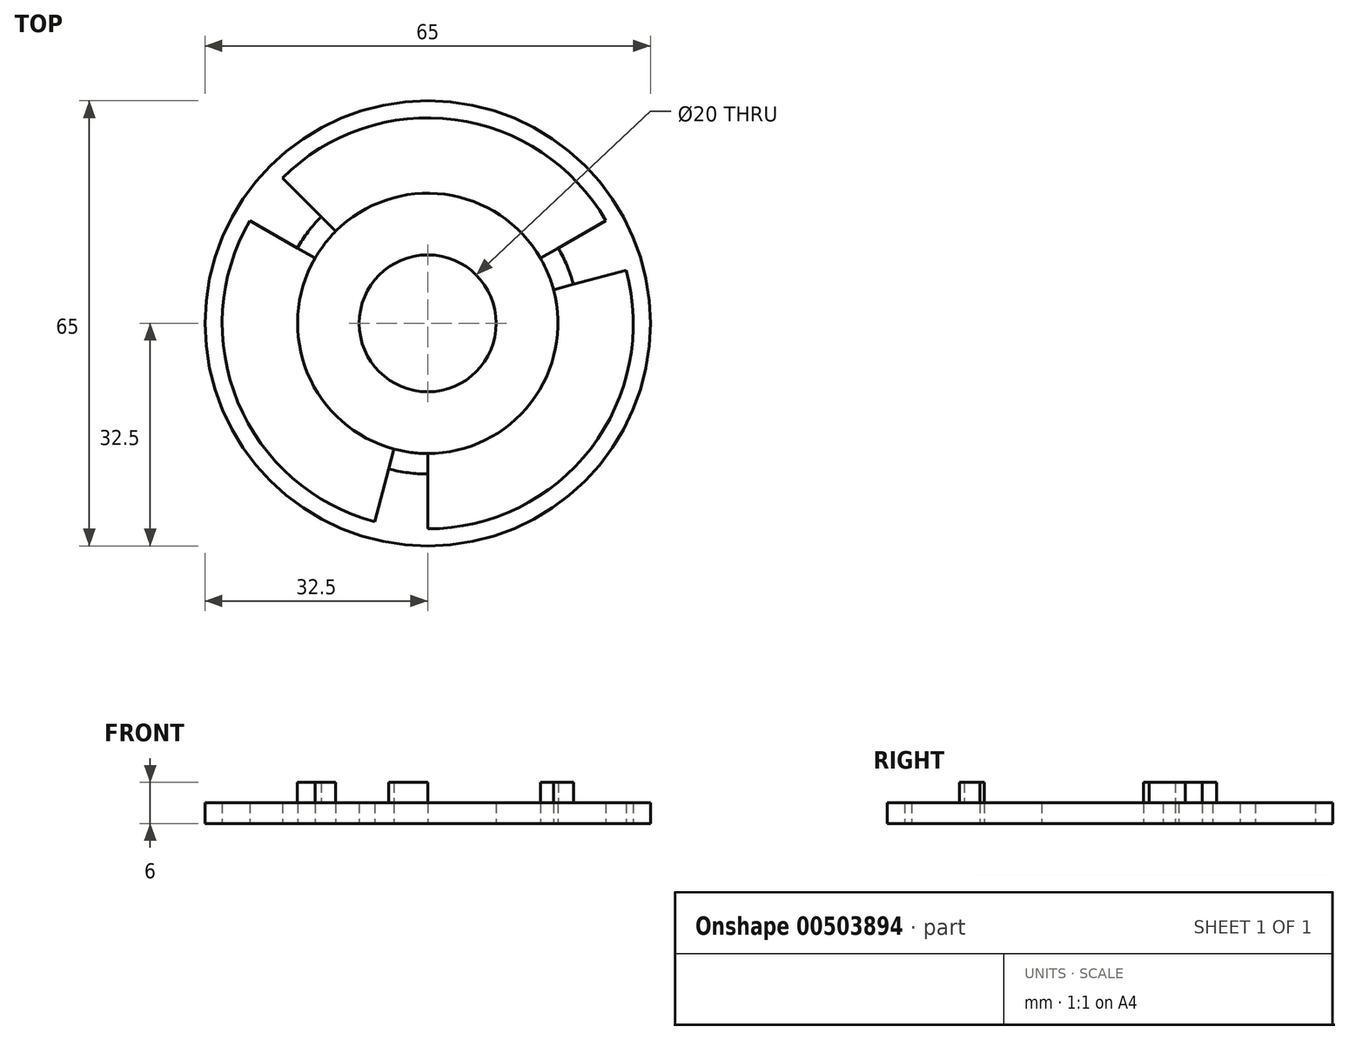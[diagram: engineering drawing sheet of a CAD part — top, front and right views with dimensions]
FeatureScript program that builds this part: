
annotation { "Feature Type Name" : "Feature", "Feature Type Description" : "" }
export const myFeature = defineFeature(function(context is Context, id is Id, definition is map)
    precondition{}
    {
        {
            var Q0;
            Q0=qCreatedBy(makeId("Top.planeOp"),FACE);
            var sketch = newSketch(context, id + "F0", { "sketchPlane" : qUnion([Q0])});
            skCircle(sketch, "E0", {"center": v(0, 0) * mm, "radius": 32.5 * mm});
            skArc(sketch, "E1", {"start": v(-25.98, 15) * mm, "mid": v(-27.72, -11.48) * mm, "end": v(-7.76, -28.98) * mm});
            skArc(sketch, "E2", {"start": v(-16.45, 9.5) * mm, "mid": v(-17.55, -7.27) * mm, "end": v(-4.92, -18.35) * mm});
            skCircle(sketch, "E3", {"center": v(0, 0) * mm, "radius": 10 * mm});
            skLineSegment(sketch, "E4", {"start": v(0, -19) * mm, "end": v(0, -30) * mm});
            skLineSegment(sketch, "E5.trimOffspring", {"start": v(-4.92, -18.35) * mm, "end": v(-7.76, -28.98) * mm});
            skLineSegment(sketch, "E6.1.0", {"start": v(16.45, 9.5) * mm, "end": v(25.98, 15) * mm});
            skLineSegment(sketch, "E6.1.1", {"start": v(18.35, 4.92) * mm, "end": v(28.98, 7.76) * mm});
            skLineSegment(sketch, "E6.2.0", {"start": v(-16.45, 9.5) * mm, "end": v(-25.98, 15) * mm});
            skLineSegment(sketch, "E6.2.1", {"start": v(-13.44, 13.44) * mm, "end": v(-21.21, 21.21) * mm});
            skArc(sketch, "E7.trimOffspring", {"start": v(16.45, 9.5) * mm, "mid": v(2.48, 18.84) * mm, "end": v(-13.44, 13.44) * mm});
            skArc(sketch, "E8.trimOffspring", {"start": v(25.98, 15) * mm, "mid": v(3.92, 29.74) * mm, "end": v(-21.21, 21.21) * mm});
            skArc(sketch, "E9.trimOffspring", {"start": v(0, -19) * mm, "mid": v(15.07, -11.57) * mm, "end": v(18.35, 4.92) * mm});
            skArc(sketch, "E10.trimOffspring", {"start": v(0, -30) * mm, "mid": v(23.8, -18.26) * mm, "end": v(28.98, 7.76) * mm});
            skSolve(sketch);
        }
        {
            var Q0;
            Q0 = qSketchRegion(id + "F0", true);
            extrude(context, id + "F1", {"entities" : qUnion([Q0]), "depth" : 3 * mm});
        }
        {
            var Q0;
            Q0=makeQuery(id+"F1.opExtrude","CAP_FACE",FACE,{"disambiguationData":[OSD([sQuery(id+"F0.wireOp",EDGE,"E0"),sQuery(id+"F0.wireOp",EDGE,"E1"),sQuery(id+"F0.wireOp",EDGE,"E2"),sQuery(id+"F0.wireOp",EDGE,"E3"),sQuery(id+"F0.wireOp",EDGE,"E4"),sQuery(id+"F0.wireOp",EDGE,"E5.trimOffspring"),sQuery(id+"F0.wireOp",EDGE,"E6.1.0"),sQuery(id+"F0.wireOp",EDGE,"E6.1.1"),sQuery(id+"F0.wireOp",EDGE,"E6.2.0"),sQuery(id+"F0.wireOp",EDGE,"E6.2.1"),sQuery(id+"F0.wireOp",EDGE,"E7.trimOffspring"),sQuery(id+"F0.wireOp",EDGE,"E8.trimOffspring"),sQuery(id+"F0.wireOp",EDGE,"E9.trimOffspring"),sQuery(id+"F0.wireOp",EDGE,"E10.trimOffspring")])],"isStart":false});
            var sketch = newSketch(context, id + "F2", { "sketchPlane" : qUnion([Q0])});
            skArc(sketch, "E11", {"start": v(-4.92, -18.35) * mm, "mid": v(-2.48, -18.84) * mm, "end": v(0, -19) * mm});
            skArc(sketch, "E12", {"start": v(-5.7, -21.25) * mm, "mid": v(-2.87, -21.81) * mm, "end": v(0, -22) * mm});
            skLineSegment(sketch, "E13.0", {"start": v(-16.45, 9.5) * mm, "end": v(-19.05, 11) * mm});
            skLineSegment(sketch, "E14.0", {"start": v(-13.44, 13.44) * mm, "end": v(-15.56, 15.56) * mm});
            skLineSegment(sketch, "E15.0", {"start": v(16.45, 9.5) * mm, "end": v(19.05, 11) * mm});
            skLineSegment(sketch, "E16.0", {"start": v(18.35, 4.92) * mm, "end": v(21.25, 5.7) * mm});
            skLineSegment(sketch, "E17.0", {"start": v(0, -19) * mm, "end": v(0, -22) * mm});
            skLineSegment(sketch, "E18.0", {"start": v(-4.92, -18.35) * mm, "end": v(-5.7, -21.25) * mm});
            skPoint(sketch, "E19.orphan", {"position": v(-25.98, 15) * mm});
            skPoint(sketch, "E20.orphan", {"position": v(-21.21, 21.21) * mm});
            skPoint(sketch, "E21.orphan", {"position": v(25.98, 15) * mm});
            skPoint(sketch, "E22.orphan", {"position": v(28.98, 7.76) * mm});
            skPoint(sketch, "E23.orphan", {"position": v(0, -30) * mm});
            skPoint(sketch, "E24.orphan", {"position": v(-7.76, -28.98) * mm});
            skArc(sketch, "E25.trimOffspring", {"start": v(-15.56, 15.56) * mm, "mid": v(-17.45, 13.4) * mm, "end": v(-19.05, 11) * mm});
            skArc(sketch, "E26.trimOffspring", {"start": v(-13.44, 13.44) * mm, "mid": v(-15.07, 11.57) * mm, "end": v(-16.45, 9.5) * mm});
            skArc(sketch, "E27.trimOffspring", {"start": v(18.35, 4.92) * mm, "mid": v(17.55, 7.27) * mm, "end": v(16.45, 9.5) * mm});
            skArc(sketch, "E28.trimOffspring", {"start": v(21.25, 5.7) * mm, "mid": v(20.33, 8.42) * mm, "end": v(19.05, 11) * mm});
            skSolve(sketch);
        }
        {
            var Q0;
            Q0 = qSketchRegion(id + "F2", true);
            extrude(context, id + "F3", {"entities" : qUnion([Q0]), "operationType" : NewBodyOperationType.ADD, "depth" : 3 * mm});
        }
    });
